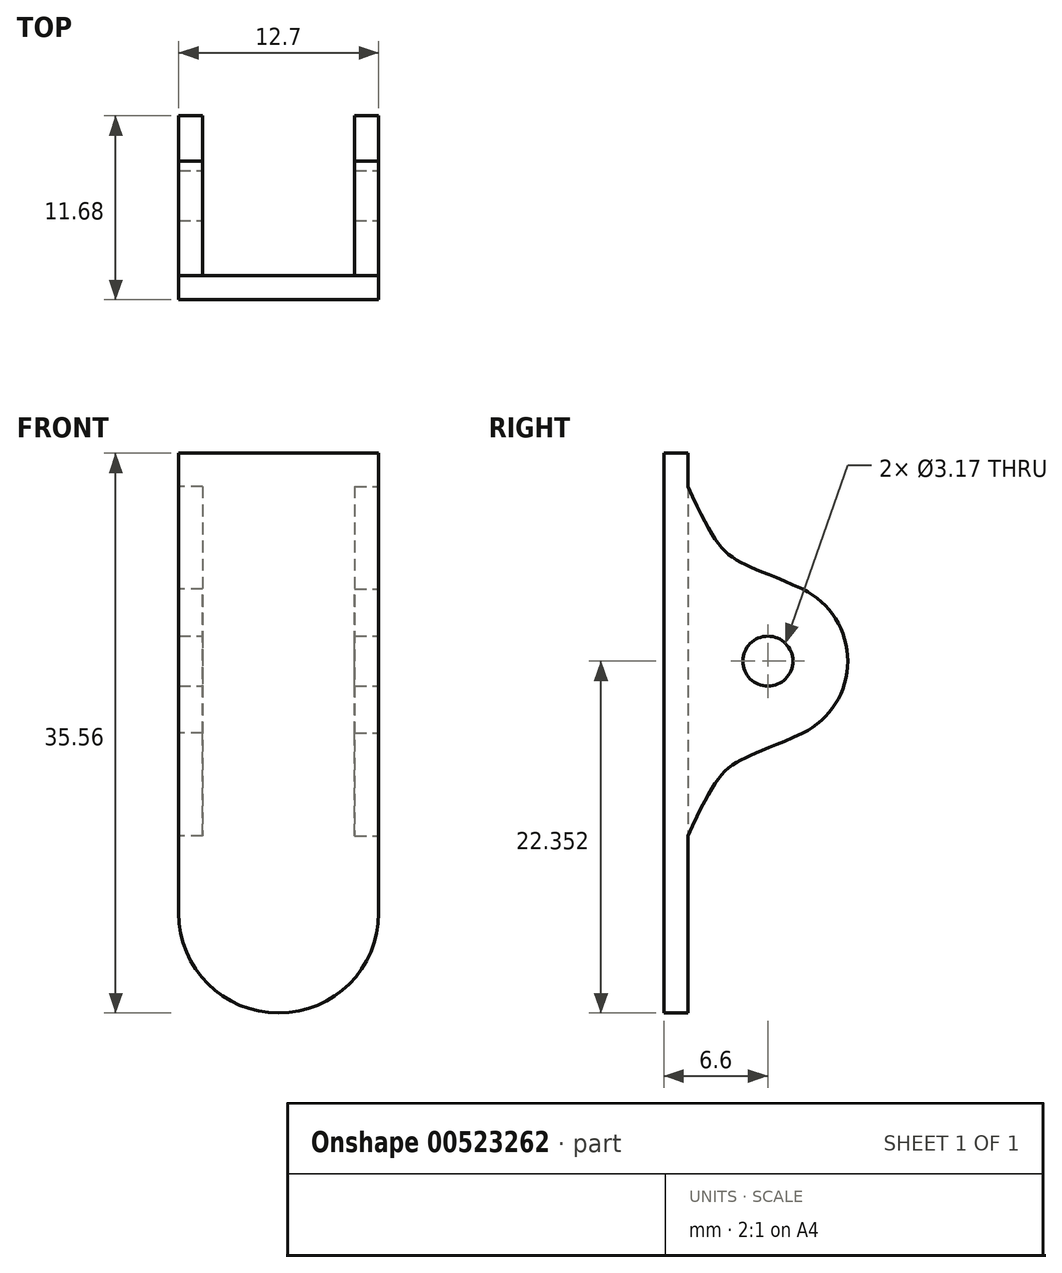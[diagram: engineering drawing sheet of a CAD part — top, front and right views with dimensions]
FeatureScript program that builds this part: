
annotation { "Feature Type Name" : "Feature", "Feature Type Description" : "" }
export const myFeature = defineFeature(function(context is Context, id is Id, definition is map)
    precondition{}
    {
        {
            var Q0;
            Q0=qCreatedBy(makeId("Front.planeOp"),FACE);
            var sketch = newSketch(context, id + "F0", { "sketchPlane" : qUnion([Q0])});
            skLineSegment(sketch, "E0.bottom", {"start": v(-6.35, 17.78) * mm, "end": v(6.35, 17.78) * mm});
            skLineSegment(sketch, "E0.top", {"start": v(0, -17.78) * mm, "end": v(0, -17.78) * mm});
            skLineSegment(sketch, "E0.left", {"start": v(-6.35, 17.78) * mm, "end": v(-6.35, -11.43) * mm});
            skLineSegment(sketch, "E0.right", {"start": v(6.35, 17.78) * mm, "end": v(6.35, -11.43) * mm});
            skPoint(sketch, "E0.middle", {"position": v(0, 0) * mm});
            skPoint(sketch, "E1.visualSharp", {"position": v(6.35, -17.78) * mm});
            skArc(sketch, "E1.filletArc", {"start": v(0, -17.78) * mm, "mid": v(4.5, -15.92) * mm, "end": v(6.35, -11.43) * mm});
            skPoint(sketch, "E2.visualSharp", {"position": v(-6.35, -17.78) * mm});
            skArc(sketch, "E2.filletArc", {"start": v(-6.35, -11.43) * mm, "mid": v(-4.5, -15.92) * mm, "end": v(0, -17.78) * mm});
            skSolve(sketch);
        }
        {
            var Q0;
            Q0=makeQuery(id+"F0.imprint","IMPRINT",FACE,{"disambiguationData":[TD([[makeQuery(id+"F0.imprint","IMPRINT",EDGE,{"derivedFrom":sQuery(id+"F0.wireOp",EDGE,"E0.bottom")}),-1.0]])]});
            extrude(context, id + "F1", {"entities" : qUnion([Q0]), "depth" : 1.52 * mm, "offsetDistance" : 25.4 * mm});
        }
        {
            var Q0;
            Q0=makeQuery(id+"F1.opExtrude","SWEPT_FACE",FACE,{"disambiguationData":[OSD([sQuery(id+"F0.wireOp",EDGE,"E0.right")])]});
            var sketch = newSketch(context, id + "F2", { "sketchPlane" : qUnion([Q0])});
            skArc(sketch, "E3", {"start": v(7.3, 0) * mm, "mid": v(10.16, 4.57) * mm, "end": v(7.3, 9.14) * mm});
            skFitSpline(sketch, "E4", {"points": [v(0, -6.53) * mm, v(7.3, 0) * mm], "startDerivative": vector(7.18, 15.82) * mm, "endDerivative": vector(14.7, 6.67) * mm});
            skLineSegment(sketch, "E5", {"start": v(0, -6.53) * mm, "end": v(0, 15.68) * mm});
            skLineSegment(sketch, "E6", {"start": v(0, 4.57) * mm, "end": v(5.08, 4.57) * mm, "construction": true});
            skFitSpline(sketch, "E7.MirrorCS", {"points": [v(0, 15.68) * mm, v(7.3, 9.14) * mm], "startDerivative": vector(7.18, -15.82) * mm, "endDerivative": vector(14.7, -6.67) * mm});
            skSolve(sketch);
        }
        {
            var Q0;
            Q0 = qSketchRegion(id + "F2", true);
            extrude(context, id + "F3", {"entities" : qUnion([Q0]), "oppositeDirection" : true, "depth" : 1.52 * mm, "offsetDistance" : 25.4 * mm});
        }
        {
            var Q0;
            Q0=makeQuery(id+"F3.opExtrude","SWEPT_BODY",BODY,{"disambiguationData":[OSD([sQuery(id+"F2.wireOp",EDGE,"E3"),sQuery(id+"F2.wireOp",EDGE,"E4"),sQuery(id+"F2.wireOp",EDGE,"E5"),sQuery(id+"F2.wireOp",EDGE,"E7.MirrorCS")])]});
            var Q1;
            Q1=qCreatedBy(makeId("Right.planeOp"),FACE);
            mirror(context, id + "F4", {"operationType" : NewBodyOperationType.ADD, "entities" : qUnion([Q0]), "mirrorPlane" : qUnion([Q1])});
        }
        {
            var Q0;
            Q0=makeQuery(id+"F4.boolean.opBoolean","MERGE",FACE,{"derivedFrom":[makeQuery(id+"F1.opExtrude","SWEPT_FACE",FACE,{"disambiguationData":[OSD([sQuery(id+"F0.wireOp",EDGE,"E0.right")])]}),makeQuery(id+"F3.opExtrude","CAP_FACE",FACE,{"disambiguationData":[OSD([sQuery(id+"F2.wireOp",EDGE,"E3"),sQuery(id+"F2.wireOp",EDGE,"E4"),sQuery(id+"F2.wireOp",EDGE,"E5"),sQuery(id+"F2.wireOp",EDGE,"E7.MirrorCS")])],"isStart":true})]});
            var sketch = newSketch(context, id + "F5", { "sketchPlane" : qUnion([Q0])});
            skPoint(sketch, "E8", {"position": v(5.08, 4.57) * mm});
            skSolve(sketch);
        }
        {
            var Q0;
            Q0=sQuery(id+"F5.wireOp",VERTEX,"E8");
            var Q1;
            Q1=makeQuery(id+"F1.opExtrude","SWEPT_BODY",BODY,{"disambiguationData":[OSD([sQuery(id+"F0.wireOp",EDGE,"E0.bottom"),sQuery(id+"F0.wireOp",EDGE,"E0.left"),sQuery(id+"F0.wireOp",EDGE,"E0.right"),sQuery(id+"F0.wireOp",EDGE,"E1.filletArc"),sQuery(id+"F0.wireOp",EDGE,"E2.filletArc")])]});
            hole(context, id + "F6", {"style" : HoleStyle.SIMPLE, "endStyle" : HoleEndStyle.THROUGH, "holeDiameter" : 3.17 * mm, "isTappedThrough" : true, "tappedDepth" : 12.7 * mm, "tapClearance" : 3, "locations" : qUnion([Q0]), "scope" : qUnion([Q1])});
        }
    });
